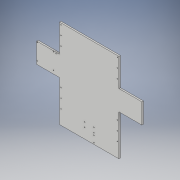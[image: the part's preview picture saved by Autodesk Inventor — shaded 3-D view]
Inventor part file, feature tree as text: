
AUTODESK INVENTOR PART (.ipt)
format: ipt  version: 2019 (Build 230136000, 136)  size: 226,816 bytes
history: native  units: in
note: dims shown in document units (in); Inventor stores cm internally (conversion verified against a paired STEP export)
features: extrude x5, sketch x5, plane x2
ambient origin geometry x8: Origin, YZ Plane, XZ Plane, XY Plane, X Axis, Y Axis, Z Axis, Center Point
bodies: Solid1 (feature_tree)
feature tree (12):
  plane  "Work Plane32"
  extrude  "Extrusion20"  Depth=0.25in TaperAngle=0.0deg
  plane  "Work Plane28"
  extrude  "Extrusion21"  Depth=3.25in
  extrude  "Extrusion22"  Depth=0.2in
  extrude  "Extrusion23"  Depth=0.2in
  extrude  "Extrusion24"  Depth=0.25in
  sketch  "Sketch36"  dims[d408=0.25in d409=0.0in d410=0.25in d411=0.0in]
  sketch  "Sketch38"  dims[d412=3.25in d413=10.0in]
  sketch  "Sketch39"  dims[d414=1.25in d415=0.2in]
  sketch  "Sketch40"  dims[d416=0.2in d417=0.2in]
  sketch  "Sketch41"  dims[d418=0.25in d419=0.0in d420=0.25in d421=0.25in d422=1.5in d423=1.5in d424=0.25in d425=0.25in d426=1.5in d427=1.5in d428=2.3in d429=1.5in d430=1.5in d431=0.25in d432=0.25in d433=0.25in d434=0.14in d435=0.14in d436=0.14in d437=0.14in d438=0.14in d439=0.14in d440=0.14in d441=0.14in d442=0.14in d443=0.14in d444=0.14in d445=0.14in d446=0.25in d447=0.0in d448=1.45in d449=0.25in d450=0.0in d284=1.0in d285=1.0in]
